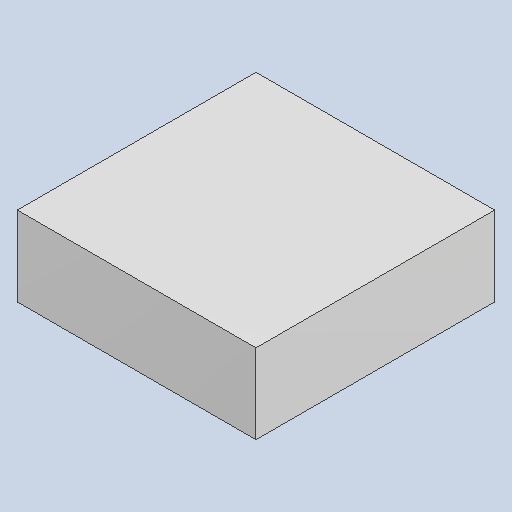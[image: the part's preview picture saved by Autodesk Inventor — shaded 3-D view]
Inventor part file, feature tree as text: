
AUTODESK INVENTOR PART (.ipt)
format: ipt  version: 2023.4 (Build 274418000, 418)  size: 79,872 bytes
history: native  units: mm
features: extrude x1
ambient origin geometry x8: Origin, YZ Plane, XZ Plane, XY Plane, X Axis, Y Axis, Z Axis, Center Point
bodies: Solid1 (feature_tree)
feature tree (1):
  extrude  "Extruded_23"  [1 undecoded]
note: 1 required parameter value undecoded (feature->parameter linkage not recoverable at this tier; creation-order binding heuristic only, values carry confidence <= 0.55)
